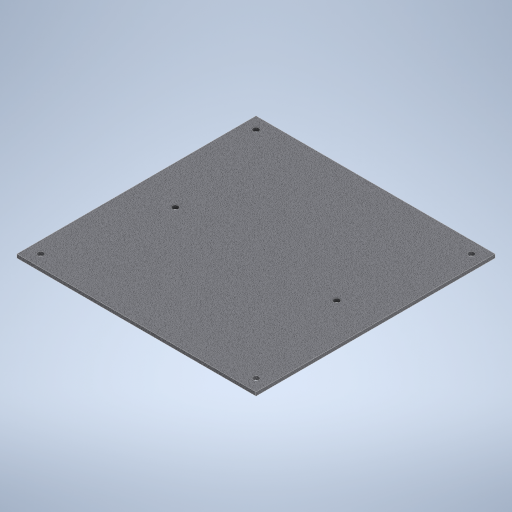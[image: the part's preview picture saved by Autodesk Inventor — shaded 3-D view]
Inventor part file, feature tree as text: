
AUTODESK INVENTOR PART (.ipt)
format: ipt  version: 2023 (Build 270158000, 158)  size: 348,672 bytes
history: native  units: mm
features: sketch x3, hole x2, other x1, extrude x1
ambient origin geometry x8: Origin, YZ Plane, XZ Plane, XY Plane, X Axis, Y Axis, Z Axis, Center Point
bodies: Body1 (feature_tree)
feature tree (7):
  other  "Sólido1"
  extrude  "Extrusão1"  Depth=200.0mm
  hole  "Furo1"  [1 undecoded]
  hole  "Furo2"  [1 undecoded]
  sketch  "Esboço1"  dims[d0=200.0mm d1=200.0mm]
  sketch  "Esboço2"  dims[d2=3.0625mm d3=0.0mm d4=10.0mm]
  sketch  "Esboço3"  dims[d5=10.0mm d6=10.0mm d7=10.0mm d8=10.0mm d9=10.0mm d10=10.0mm d11=10.0mm d12=5.0mm d13=6.0mm d14=4.0mm d15=2.0mm d16=90.0deg d17=0.5mm d18=20.594885mm d22=135.0mm d27=5.0mm d28=6.0mm d29=4.0mm d30=2.0mm d31=90.0deg d32=0.5mm d33=20.594885mm d34=200.0mm d35=200.0mm d46=200.0mm d49=100.0mm d50=0.0mm d51=32.5mm]
note: 2 required parameter values undecoded (feature->parameter linkage not recoverable at this tier; creation-order binding heuristic only, values carry confidence <= 0.55)
